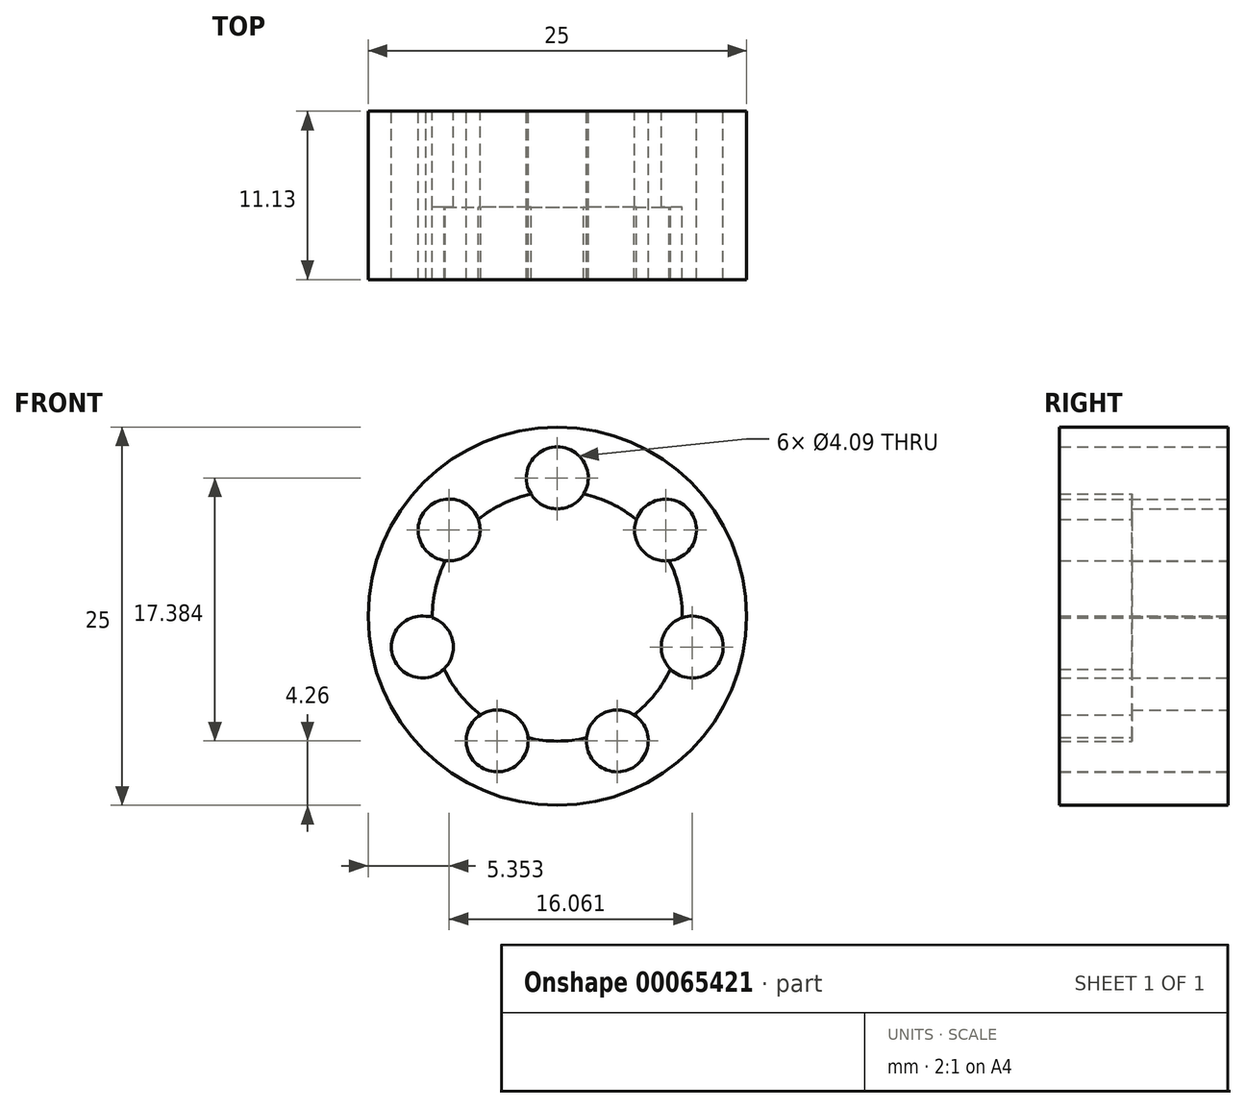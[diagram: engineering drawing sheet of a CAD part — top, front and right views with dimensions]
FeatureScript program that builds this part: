
annotation { "Feature Type Name" : "Feature", "Feature Type Description" : "" }
export const myFeature = defineFeature(function(context is Context, id is Id, definition is map)
    precondition{}
    {
        {
            var Q0;
            Q0=qCreatedBy(makeId("Front.planeOp"),FACE);
            var sketch = newSketch(context, id + "F0", { "sketchPlane" : qUnion([Q0])});
            skCircle(sketch, "E0", {"center": v(0, 0) * mm, "radius": 12.5 * mm});
            skCircle(sketch, "E1", {"center": v(0, 0) * mm, "radius": 8.26 * mm});
            skLineSegment(sketch, "E2.bottom", {"start": v(0, 0) * mm, "end": v(-8.92, 0) * mm});
            skLineSegment(sketch, "E2.top", {"start": v(0, -2.03) * mm, "end": v(-8.92, -2.03) * mm});
            skLineSegment(sketch, "E2.left", {"start": v(0, 0) * mm, "end": v(0, -2.03) * mm});
            skLineSegment(sketch, "E2.right", {"start": v(-8.92, 0) * mm, "end": v(-8.92, -2.03) * mm});
            skCircle(sketch, "E3", {"center": v(-8.92, -2.03) * mm, "radius": 2.04 * mm});
            skCircle(sketch, "E4.1.0", {"center": v(-3.97, -8.24) * mm, "radius": 2.04 * mm});
            skCircle(sketch, "E4.2.0", {"center": v(3.96, -8.24) * mm, "radius": 2.04 * mm});
            skCircle(sketch, "E4.3.0", {"center": v(8.91, -2.04) * mm, "radius": 2.04 * mm});
            skCircle(sketch, "E4.4.0", {"center": v(7.15, 5.7) * mm, "radius": 2.04 * mm});
            skCircle(sketch, "E4.5.0", {"center": v(0, 9.14) * mm, "radius": 2.04 * mm});
            skCircle(sketch, "E4.6.0", {"center": v(-7.15, 5.7) * mm, "radius": 2.04 * mm});
            skSolve(sketch);
        }
        {
            var Q0;
            Q0 = qSketchRegion(id + "F0", true);
            extrude(context, id + "F1", {"entities" : qUnion([Q0]), "depth" : 11.13 * mm});
        }
        {
            var Q0;
            {var subQ0=sQuery(id+"F0.wireOp",EDGE,"E2.left");Q0=makeQuery(id+"F0.imprint","IMPRINT",FACE,{"disambiguationData":[TD([[makeQuery(id+"F0.imprint","IMPRINT",EDGE,{"derivedFrom":subQ0}),1.0]])]});}
            var Q1;
            {var subQ0=sQuery(id+"F0.wireOp",EDGE,"E2.left");Q1=makeQuery(id+"F0.imprint","IMPRINT",FACE,{"disambiguationData":[TD([[makeQuery(id+"F0.imprint","IMPRINT",EDGE,{"derivedFrom":subQ0}),-1.0]])]});}
            extrude(context, id + "F2", {"entities" : qUnion([Q0, Q1]), "operationType" : NewBodyOperationType.ADD, "depth" : 6.35 * mm});
        }
    });
